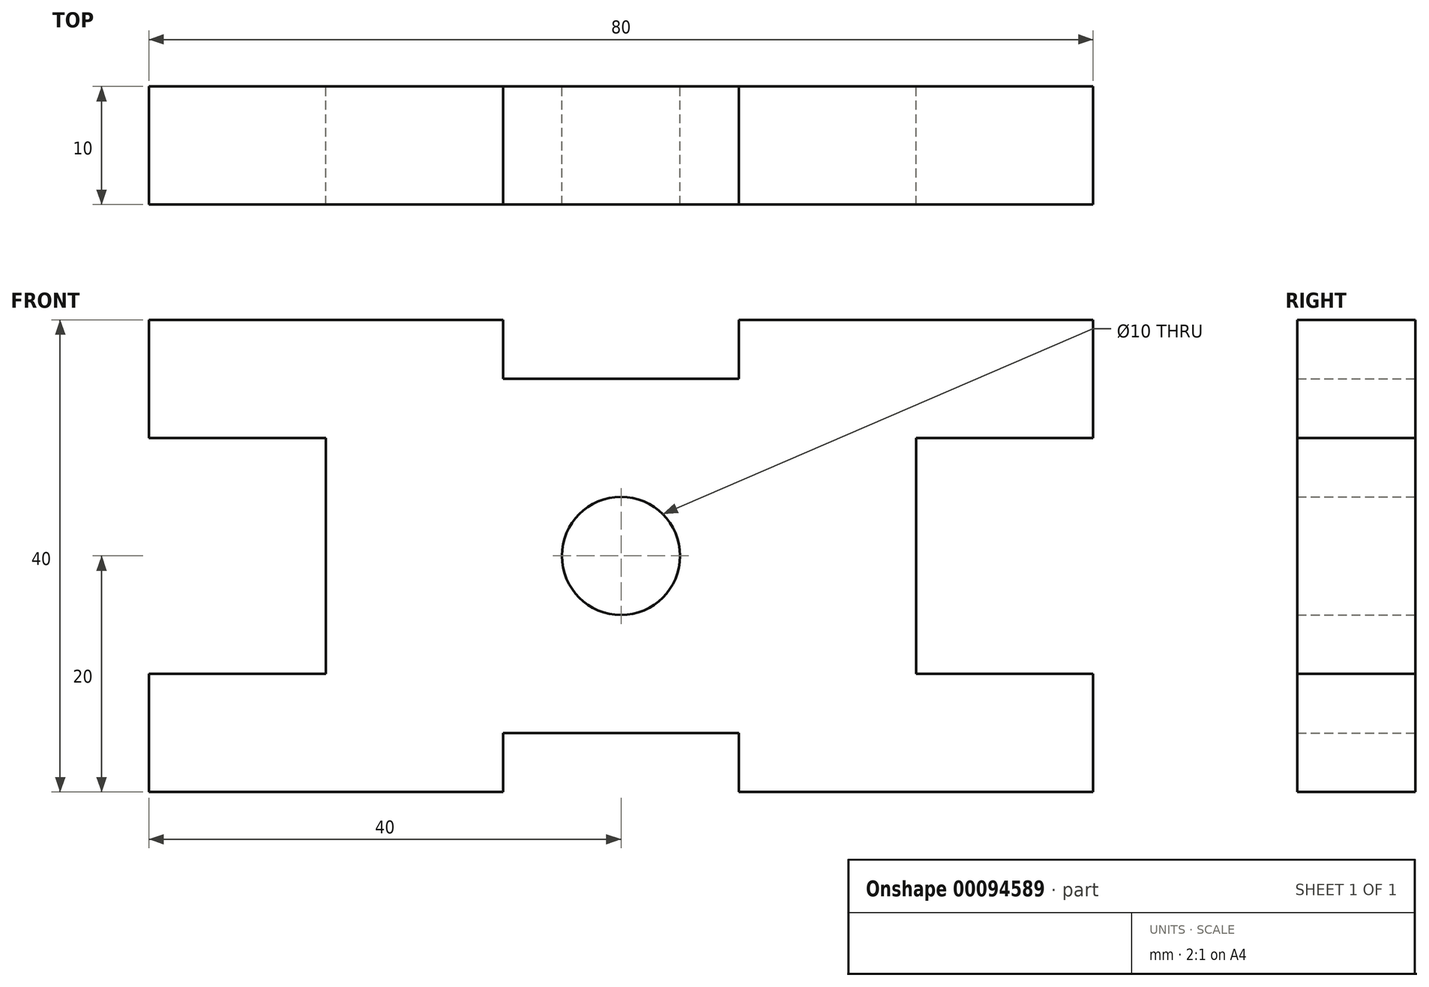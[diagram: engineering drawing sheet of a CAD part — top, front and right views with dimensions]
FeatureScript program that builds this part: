
annotation { "Feature Type Name" : "Feature", "Feature Type Description" : "" }
export const myFeature = defineFeature(function(context is Context, id is Id, definition is map)
    precondition{}
    {
        {
            var Q0;
            Q0=qCreatedBy(makeId("Front.planeOp"),FACE);
            var sketch = newSketch(context, id + "F0", { "sketchPlane" : qUnion([Q0])});
            skLineSegment(sketch, "E0", {"start": v(0, 15) * mm, "end": v(0, 0) * mm});
            skLineSegment(sketch, "E1", {"start": v(25, 0) * mm, "end": v(25, 10) * mm});
            skLineSegment(sketch, "E2", {"start": v(25, 10) * mm, "end": v(40, 10) * mm});
            skLineSegment(sketch, "E3", {"start": v(40, 10) * mm, "end": v(40, 20) * mm});
            skLineSegment(sketch, "E4", {"start": v(40, 20) * mm, "end": v(10, 20) * mm});
            skLineSegment(sketch, "E5", {"start": v(10, 20) * mm, "end": v(10, 15) * mm});
            skLineSegment(sketch, "E6", {"start": v(10, 15) * mm, "end": v(0, 15) * mm});
            skLineSegment(sketch, "E7.MirrorCS", {"start": v(-10, 20) * mm, "end": v(-10, 15) * mm});
            skLineSegment(sketch, "E8.MirrorCS", {"start": v(-10, 15) * mm, "end": v(0, 15) * mm});
            skLineSegment(sketch, "E9.MirrorCS", {"start": v(-25, 0) * mm, "end": v(-25, 10) * mm});
            skLineSegment(sketch, "E10.MirrorCS", {"start": v(-25, 10) * mm, "end": v(-40, 10) * mm});
            skLineSegment(sketch, "E11.MirrorCS", {"start": v(-40, 10) * mm, "end": v(-40, 20) * mm});
            skLineSegment(sketch, "E12.MirrorCS", {"start": v(-40, 20) * mm, "end": v(-10, 20) * mm});
            skLineSegment(sketch, "E13.MirrorCS", {"start": v(10, -20) * mm, "end": v(10, -15) * mm});
            skLineSegment(sketch, "E14.MirrorCS", {"start": v(-10, -20) * mm, "end": v(-10, -15) * mm});
            skLineSegment(sketch, "E15.MirrorCS", {"start": v(-40, -20) * mm, "end": v(-10, -20) * mm});
            skLineSegment(sketch, "E16.MirrorCS", {"start": v(25, -10) * mm, "end": v(40, -10) * mm});
            skLineSegment(sketch, "E17.MirrorCS", {"start": v(-40, -10) * mm, "end": v(-40, -20) * mm});
            skLineSegment(sketch, "E18.MirrorCS", {"start": v(10, -15) * mm, "end": v(0, -15) * mm});
            skLineSegment(sketch, "E19.MirrorCS", {"start": v(25, 0) * mm, "end": v(25, -10) * mm});
            skLineSegment(sketch, "E20.MirrorCS", {"start": v(40, -20) * mm, "end": v(10, -20) * mm});
            skLineSegment(sketch, "E21.MirrorCS", {"start": v(-25, -10) * mm, "end": v(-40, -10) * mm});
            skLineSegment(sketch, "E22.MirrorCS", {"start": v(-10, -15) * mm, "end": v(0, -15) * mm});
            skLineSegment(sketch, "E23.MirrorCS", {"start": v(0, -15) * mm, "end": v(0, 0) * mm});
            skLineSegment(sketch, "E24.MirrorCS", {"start": v(-25, 0) * mm, "end": v(-25, -10) * mm});
            skLineSegment(sketch, "E25.MirrorCS", {"start": v(40, -10) * mm, "end": v(40, -20) * mm});
            skCircle(sketch, "E26", {"center": v(0, 0) * mm, "radius": 5 * mm});
            skSolve(sketch);
        }
        {
            var Q0;
            Q0 = qSketchRegion(id + "F0", true);
            extrude(context, id + "F1", {"entities" : qUnion([Q0]), "depth" : 10 * mm});
        }
    });
